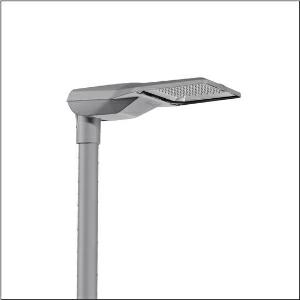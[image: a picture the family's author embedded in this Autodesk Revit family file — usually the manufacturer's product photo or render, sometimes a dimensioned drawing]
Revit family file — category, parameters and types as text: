
# Revit family: streetlight_sl_21_midi___pl52_5xe7h43a08mb_148e
name_source: partatom
category: Lighting Fixtures
units: mm (PartAtom-declared; Revit-internal decimal feet)

## family parameters
Cut with Voids When Loaded = No
Host = Face
Light Source = No
Part Type = Normal
Room Calculation Point = No
Round Connector Dimension = Use Diameter
Shared = No

## types (1)
- --- (1 x LED, 19830 lm, 147 W, 4000K)
    Apparent Load = 147 VA
    CIE Flux Codes = 27 59 98 100 100
    Color Rendering = 70
    Color Temperature = 4000K
    Default Elevation = 1800 mm
    Description = Streetlight SL 21 midi, mast luminaire, primary light control with lens, of PMMA, primary optical cover: cover, of toughened safety glass, transparent, light distribution: PL52, light emission: direct distribution, primary light characteristic: asymmetric, installation type: post-top, side-entry, LED, 3G 1.5mm², High Power LED, rated luminous flux: 19.830lm, luminous efficacy: 135lm/W, light colour: 740, colour temperature: 4000K, control: overheat protection, constant luminous flux control, time-dependent luminous flux control, flexible luminous flux parameterisation, mains connection: 220..240V, AC, 50/60Hz, connection cable pre-assembled, cable length: 12,5m, wiring characteristics: H07RN-F, start of lifetime: 147W, end of service life: 155W, reduction: 64W, luminaire housing, of diecast aluminium, powder-coated, Siteco® metallic grey (DB 702S), corrosivity category C5 mid according to DIN EN ISO 12944, please order mast flange separately, inclination adjustable: 0°, 5°, 10°, 15°, sealing non-destructively replaceable, multi-level sealing system, length: 644mm, width: 335mm, height: 110mm, mast flange for spigot size: 42mm (side-entry): 5XC10008XM4, 60/48mm (side-entry/post-top): 5XC10108XM2, 76/60mm (side-entry/post-top): 5XC10108XM1, protection rating (complete): IP66, insulation class (complete): insulation class II (safety insulation), certification: CE, ENEC, ENEC+, VDE, impact resistance: IK09, permissible operating ambient temperature for outdoor applications: -40..+50°C, standard-compliant lighting for roads and squares, packaging unit: 1 piece

Light Distribution: PL52
    Height = 111 mm
    Lamp = 1 x LED
    Lamp Light Flux = 19830 lm
    Lamp Power = 147 W
    Lamp count = 1
    Length = 644 mm
    Luminous efficacy = 135 lm/W
    Manufacturer = Siteco
    ModVariant = No
    Model = 5XE7H43A08MB
    Number of Poles = 1
    OnlyDefault = Yes
    Power Factor = 1
    Product Name = Streetlight SL 21 midi | PL52
    Product group = mast luminaire | pylon top
    ProductGroupID = 6100
    Protection Class = Protection class II
    Protection Degree = IP 66
    RLX_Detail_Level = 1
    RLX_Emergency_Light_Flux = 0 lm
    RLX_Emergency_Type = 0
    RLX_Emergency_Type_DB = No
    RlxData = <blob elided: 99833 chars, md5=9a205c09>
    Socket = socket
    Standby Power = 0 W
    System Light Flux = 19830 lm
    System Power = 147 W
    Type Comments = factory setting: luminous flux: 100 % | Output Level: 100 % | 750 mA
    Type Image = l_1004298.jpg
    URL = http://relux.com
    VarID = @adj_124387
    Voltage = 0 V
    Weight = 0.00 kg
    Width = 336 mm

## geometry (parser evidence)
native form markers: Blend x4, Sweep x9
no freeform markers — native parametric forms only
